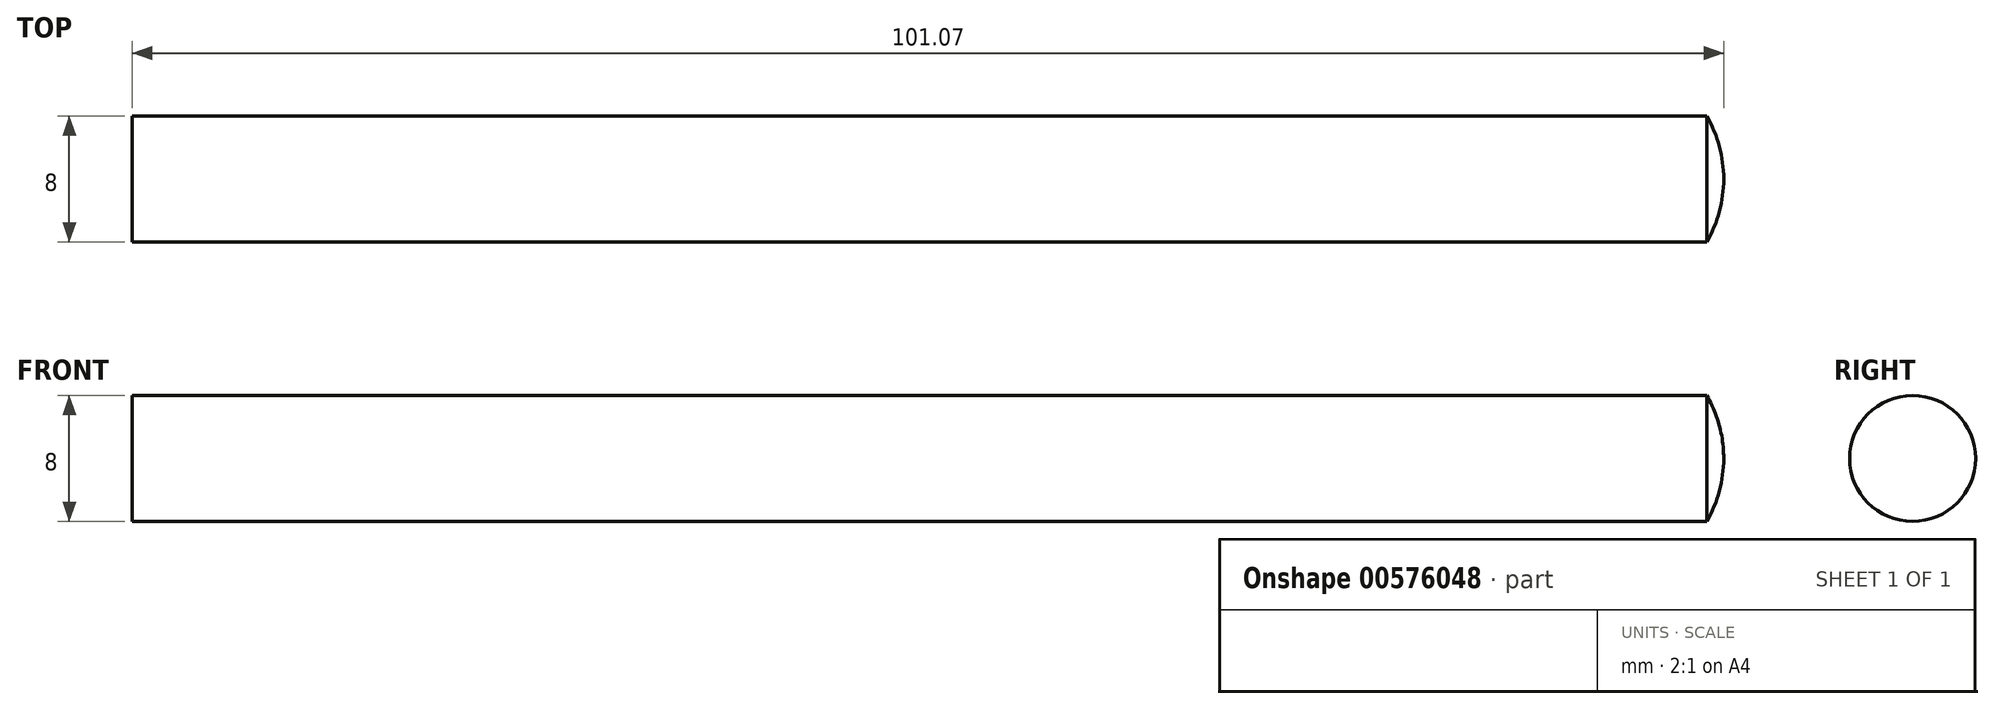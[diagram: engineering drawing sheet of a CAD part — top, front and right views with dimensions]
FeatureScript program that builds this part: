
annotation { "Feature Type Name" : "Feature", "Feature Type Description" : "" }
export const myFeature = defineFeature(function(context is Context, id is Id, definition is map)
    precondition{}
    {
        {
            var Q0;
            Q0=qCreatedBy(makeId("Right.planeOp"),FACE);
            var sketch = newSketch(context, id + "F0", { "sketchPlane" : qUnion([Q0])});
            skCircle(sketch, "E0", {"center": v(0, 0) * mm, "radius": 4 * mm});
            skSolve(sketch);
        }
        {
            var Q0;
            Q0=makeQuery(id+"F0.imprint","IMPRINT",FACE,{"disambiguationData":[TD([[makeQuery(id+"F0.imprint","IMPRINT",EDGE,{"derivedFrom":sQuery(id+"F0.wireOp",EDGE,"E0")}),1.0]])]});
            extrude(context, id + "F1", {"entities" : qUnion([Q0]), "endBound" : BoundingType.SYMMETRIC, "depth" : 100 * mm, "offsetDistance" : 25 * mm});
        }
        {
            var Q0;
            Q0=qCreatedBy(makeId("Front.planeOp"),FACE);
            var sketch = newSketch(context, id + "F2", { "sketchPlane" : qUnion([Q0])});
            skLineSegment(sketch, "E1", {"start": v(-50, 4) * mm, "end": v(50, 4) * mm});
            skLineSegment(sketch, "E2", {"start": v(50, -4) * mm, "end": v(-50, -4) * mm});
            skLineSegment(sketch, "E3.0", {"start": v(50, 4) * mm, "end": v(50, -4) * mm});
            skArc(sketch, "E4", {"start": v(51.07, 0) * mm, "mid": v(50.8, 2.07) * mm, "end": v(50, 4) * mm});
            skLineSegment(sketch, "E5", {"start": v(0, 0) * mm, "end": v(43.07, 0) * mm});
            skLineSegment(sketch, "E6.trimOffspring", {"start": v(50, 0) * mm, "end": v(51.07, 0) * mm});
            skSolve(sketch);
        }
        {
            var Q0;
            {var subQ0=sQuery(id+"F2.wireOp",EDGE,"E4");Q0=makeQuery(id+"F2.imprint","IMPRINT",FACE,{"disambiguationData":[TD([[makeQuery(id+"F2.imprint","IMPRINT",EDGE,{"derivedFrom":subQ0}),1.0]])]});}
            var Q1;
            Q1=makeQuery(id+"F1.opExtrude","SWEPT_FACE",FACE,{"disambiguationData":[OSD([sQuery(id+"F0.wireOp",EDGE,"E0")])]});
            revolve(context, id + "F3", {"operationType" : NewBodyOperationType.ADD, "entities" : qUnion([Q0]), "axis" : qUnion([Q1]), "revolveType" : RevolveType.FULL});
        }
    });
